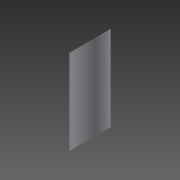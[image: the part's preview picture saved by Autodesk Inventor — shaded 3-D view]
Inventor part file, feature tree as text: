
AUTODESK INVENTOR PART (.ipt)
format: ipt  version: 2015 (Build 190159000, 159)  size: 95,744 bytes
history: native  units: mm
features: other x3, extrude x1, shell x1, sketch x1
ambient origin geometry x8: Origin, YZ Plane, XZ Plane, XY Plane, X Axis, Y Axis, Z Axis, Center Point
bodies: Body1 (feature_tree)
feature tree (6):
  other  "Bryła1"
  extrude  "Wyciągnięcie proste1"  Depth=32.0mm
  shell  "Skorupa1"  Thickness=150.0mm
  other  "Podział1"
  other  "Podział2"
  sketch  "Szkic1"
